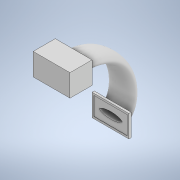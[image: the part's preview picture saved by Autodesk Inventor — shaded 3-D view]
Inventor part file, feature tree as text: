
AUTODESK INVENTOR PART (.ipt)
format: ipt  version: 2021 (Build 250183000, 183)  size: 367,616 bytes
history: native  units: mm
features: sketch x5, extrude x2, plane x1, sweep x1, shell x1
ambient origin geometry x8: Origin, YZ Plane, XZ Plane, XY Plane, X Axis, Y Axis, Z Axis, Center Point
bodies: Volumenkörper1 (feature_tree)
feature tree (10):
  extrude  "Extrusion1"  Depth=30.0mm
  sketch  "Skizze2"  dims[d2=30.0mm d3=0.0mm d4=15.0mm]
  sketch  "Skizze3"  dims[d5=25.0mm d6=18.0mm d7=7.0mm]
  plane  "Arbeitsebene1"
  extrude  "Extrusion2"  Depth=15.0mm
  sweep  "Sweeping1"
  shell  "Wandung1"  Thickness=7.0mm
  sketch  "Skizze1"  dims[d0=50.0mm d1=30.0mm]
  sketch  "Skizze4"  dims[d8=53.0mm]
  sketch  "Skizze5"  dims[d9=50.0mm d10=30.0mm d11=58.0mm d12=3.0mm d13=0.0mm d32=77.124757mm d33=117.013795mm d34=88.0mm d35=0.0mm d36=0.0mm d37=2.5mm]
